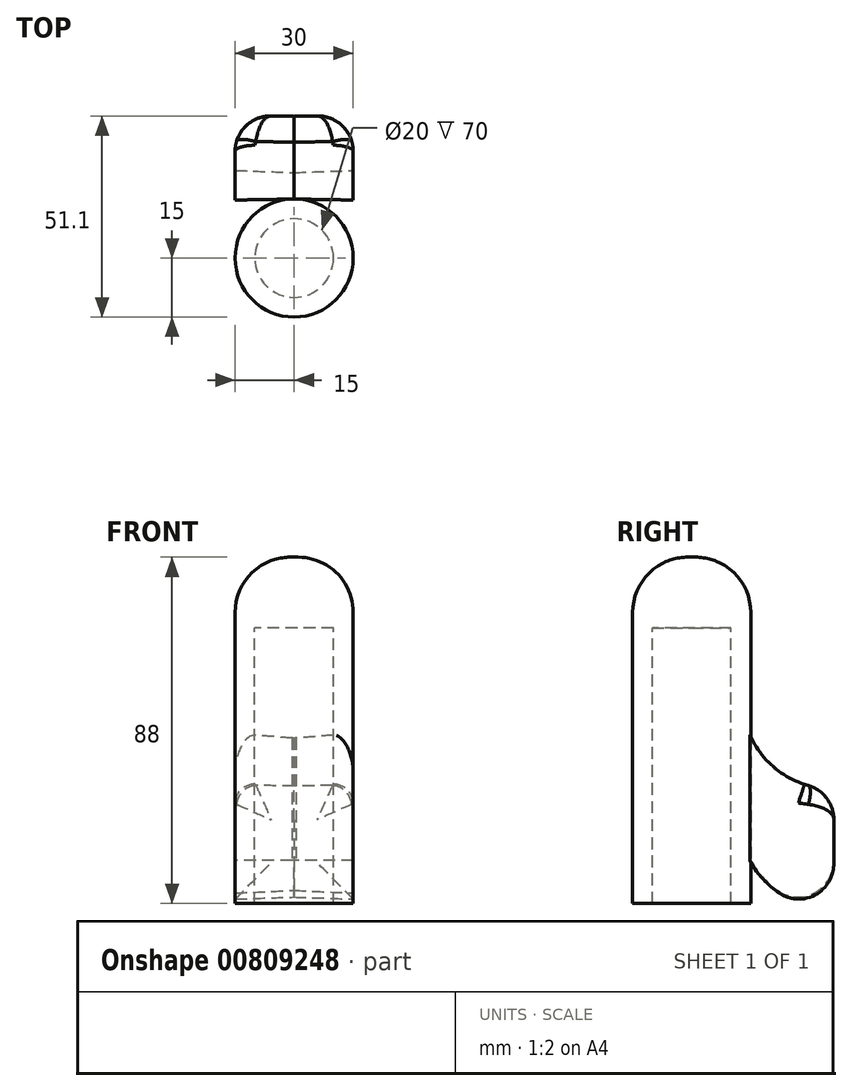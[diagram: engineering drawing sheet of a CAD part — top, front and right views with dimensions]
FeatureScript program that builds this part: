
annotation { "Feature Type Name" : "Feature", "Feature Type Description" : "" }
export const myFeature = defineFeature(function(context is Context, id is Id, definition is map)
    precondition{}
    {
        {
            var Q0;
            Q0=qCreatedBy(makeId("Top.planeOp"),FACE);
            var sketch = newSketch(context, id + "F0", { "sketchPlane" : qUnion([Q0])});
            skCircle(sketch, "E0", {"center": v(0, 0) * mm, "radius": 15 * mm});
            skCircle(sketch, "E1", {"center": v(0, 0) * mm, "radius": 10 * mm});
            skSolve(sketch);
        }
        {
            var Q0;
            Q0=makeQuery(id+"F0.imprint","IMPRINT",FACE,{"disambiguationData":[TD([[makeQuery(id+"F0.imprint","IMPRINT",EDGE,{"derivedFrom":sQuery(id+"F0.wireOp",EDGE,"E0")}),1.0]])]});
            var Q1;
            Q1=makeQuery(id+"F0.imprint","IMPRINT",FACE,{"disambiguationData":[TD([[makeQuery(id+"F0.imprint","IMPRINT",EDGE,{"derivedFrom":sQuery(id+"F0.wireOp",EDGE,"E1")}),1.0]])]});
            extrude(context, id + "F1", {"entities" : qUnion([Q0, Q1]), "depth" : 18 * mm, "offsetDistance" : 25 * mm});
        }
        {
            var Q0;
            Q0=makeQuery(id+"F1.opExtrude","CAP_EDGE",EDGE,{"disambiguationData":[OSD([sQuery(id+"F0.wireOp",EDGE,"E0")])],"isStart":false});
            fillet(context, id + "F2", {"entities" : qUnion([Q0]), "radius" : 14 * mm, "tangentPropagation" : true, "allowEdgeOverflow" : false});
        }
        {
            var Q0;
            Q0=makeQuery(id+"F0.imprint","IMPRINT",FACE,{"disambiguationData":[TD([[makeQuery(id+"F0.imprint","IMPRINT",EDGE,{"derivedFrom":sQuery(id+"F0.wireOp",EDGE,"E0")}),1.0]])]});
            extrude(context, id + "F3", {"entities" : qUnion([Q0]), "operationType" : NewBodyOperationType.ADD, "oppositeDirection" : true, "depth" : 70 * mm, "offsetDistance" : 25 * mm});
        }
        {
            var Q0;
            Q0=qCreatedBy(makeId("Right.planeOp"),FACE);
            var sketch = newSketch(context, id + "F4", { "sketchPlane" : qUnion([Q0])});
            skArc(sketch, "E2", {"start": v(15, -28) * mm, "mid": v(23.6, -37.56) * mm, "end": v(36, -41) * mm});
            skLineSegment(sketch, "E3", {"start": v(36, -41) * mm, "end": v(36, -71) * mm});
            skArc(sketch, "E4", {"start": v(15, -59) * mm, "mid": v(23.8, -67.98) * mm, "end": v(36, -71) * mm});
            skLineSegment(sketch, "E5", {"start": v(15, -28) * mm, "end": v(15, -59) * mm});
            skSolve(sketch);
        }
        {
            var Q0;
            Q0=makeQuery(id+"F4.imprint","IMPRINT",FACE,{"disambiguationData":[TD([[makeQuery(id+"F4.imprint","IMPRINT",EDGE,{"derivedFrom":sQuery(id+"F4.wireOp",EDGE,"E2")}),-1.0]])]});
            extrude(context, id + "F5", {"entities" : qUnion([Q0]), "operationType" : NewBodyOperationType.ADD, "depth" : 15 * mm, "offsetDistance" : 25 * mm, "hasDraft" : true, "draftAngle" : 1 * degree, "hasSecondDirection" : true, "secondDirectionOppositeDirection" : true, "secondDirectionDepth" : 15 * mm, "hasSecondDirectionDraft" : true, "secondDirectionDraftAngle" : 1 * degree});
        }
        {
            var Q0;
            Q0=makeQuery(id+"F5.*.split.splitOp","SPLIT",EDGE,{"derivedFrom":makeQuery(id+"F5.opExtrude","SWEPT_EDGE",EDGE,{"disambiguationData":[OSD([sQuery(id+"F4.wireOp",EDGE,"E2"),sQuery(id+"F4.wireOp",EDGE,"E3")])]})});
            var Q1;
            Q1=makeQuery(id+"F5.opExtrude","CAP_EDGE",EDGE,{"disambiguationData":[OSD([sQuery(id+"F4.wireOp",EDGE,"E3")])],"isStart":false});
            var Q2;
            Q2=makeQuery(id+"F5.*.split.splitOp","SPLIT",EDGE,{"derivedFrom":makeQuery(id+"F5.opExtrude","SWEPT_EDGE",EDGE,{"disambiguationData":[OSD([sQuery(id+"F4.wireOp",EDGE,"E3"),sQuery(id+"F4.wireOp",EDGE,"E4")])]}),"isFromBackBody":true});
            var Q3;
            Q3=makeQuery(id+"F5.opExtrude","CAP_EDGE",EDGE,{"disambiguationData":[OSD([sQuery(id+"F4.wireOp",EDGE,"E3")])],"isStart":true});
            var Q4;
            Q4=makeQuery(id+"F5.*.split.splitOp","SPLIT",EDGE,{"derivedFrom":makeQuery(id+"F5.opExtrude","SWEPT_EDGE",EDGE,{"disambiguationData":[OSD([sQuery(id+"F4.wireOp",EDGE,"E2"),sQuery(id+"F4.wireOp",EDGE,"E3")])]}),"isFromBackBody":true});
            fillet(context, id + "F6", {"entities" : qUnion([Q0, Q1, Q2, Q3, Q4]), "radius" : 9 * mm, "tangentPropagation" : true, "allowEdgeOverflow" : false});
        }
        {
            var Q0;
            {var subQ0=sQuery(id+"F4.wireOp",EDGE,"E3");Q0=makeQuery(id+"F6.opFillet","BLEND_EDGE",EDGE,{"blendedFrom":[makeQuery(id+"F5.opExtrude","CAP_EDGE",EDGE,{"disambiguationData":[OSD([subQ0])],"isStart":false}),makeQuery(id+"F5.*.split.splitOp","SPLIT",EDGE,{"derivedFrom":makeQuery(id+"F5.opExtrude","SWEPT_EDGE",EDGE,{"disambiguationData":[OSD([sQuery(id+"F4.wireOp",EDGE,"E2"),subQ0])]})})],"blendedInto":[]});}
            var Q1;
            {var subQ0=sQuery(id+"F4.wireOp",EDGE,"E3");Q1=makeQuery(id+"F6.opFillet","BLEND_EDGE",EDGE,{"blendedFrom":[makeQuery(id+"F5.opExtrude","CAP_EDGE",EDGE,{"disambiguationData":[OSD([subQ0])],"isStart":true}),makeQuery(id+"F5.*.split.splitOp","SPLIT",EDGE,{"derivedFrom":makeQuery(id+"F5.opExtrude","SWEPT_EDGE",EDGE,{"disambiguationData":[OSD([sQuery(id+"F4.wireOp",EDGE,"E2"),subQ0])]}),"isFromBackBody":true})],"blendedInto":[]});}
            fillet(context, id + "F7", {"entities" : qUnion([Q0, Q1]), "radius" : 5 * mm, "tangentPropagation" : true, "allowEdgeOverflow" : false});
        }
    });
